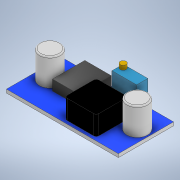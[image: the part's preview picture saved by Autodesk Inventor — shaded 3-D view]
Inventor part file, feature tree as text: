
AUTODESK INVENTOR PART (.ipt)
format: ipt  version: 2022 (Build 260153000, 153)  size: 200,704 bytes
history: native  units: in
note: dims shown in document units (in); Inventor stores cm internally (conversion verified against a paired STEP export)
features: extrude x6, sketch x6, fillet x1
ambient origin geometry x8: Origin, YZ Plane, XZ Plane, XY Plane, X Axis, Y Axis, Z Axis, Center Point
bodies: Solid1 (feature_tree)
feature tree (13):
  extrude  "Extrusion1"  Depth=0.8346in
  extrude  "Extrusion2"  Depth=0.8465in
  extrude  "Extrusion3"  Depth=0.4882in
  extrude  "Extrusion4"  Depth=0.3228in
  extrude  "Extrusion5"  Depth=0.1575in TaperAngle=0.0deg
  extrude  "Extrusion6"  Depth=0.4803in
  fillet  "Fillet1"  Radius=0.0472in
  sketch  "Sketch1"  dims[d0=1.6929in d1=0.8346in]
  sketch  "Sketch2"  dims[d2=0.4173in d3=0.8465in]
  sketch  "Sketch3"  dims[d4=0.0516in d5=0.0in d6=0.4882in]
  sketch  "Sketch4"  dims[d7=0.3996in d8=0.3228in]
  sketch  "Sketch5"  dims[d9=0.374in d10=0.1575in d11=0.0in]
  sketch  "Sketch6"  dims[d12=0.4803in d13=0.4803in d14=0.0472in d15=0.3819in d16=0.0394in d17=0.2913in d18=0.0in d19=0.1697in d20=0.3728in d21=0.3689in d22=0.0197in d23=0.3937in d24=0.0in d25=0.0886in d26=0.0472in d27=0.0472in d28=0.0634in d29=0.0in d30=0.315in d31=0.315in d32=0.4657in d33=0.1799in d34=0.2055in d35=0.4516in d36=0.4134in d37=0.0in d38=0.0197in]
